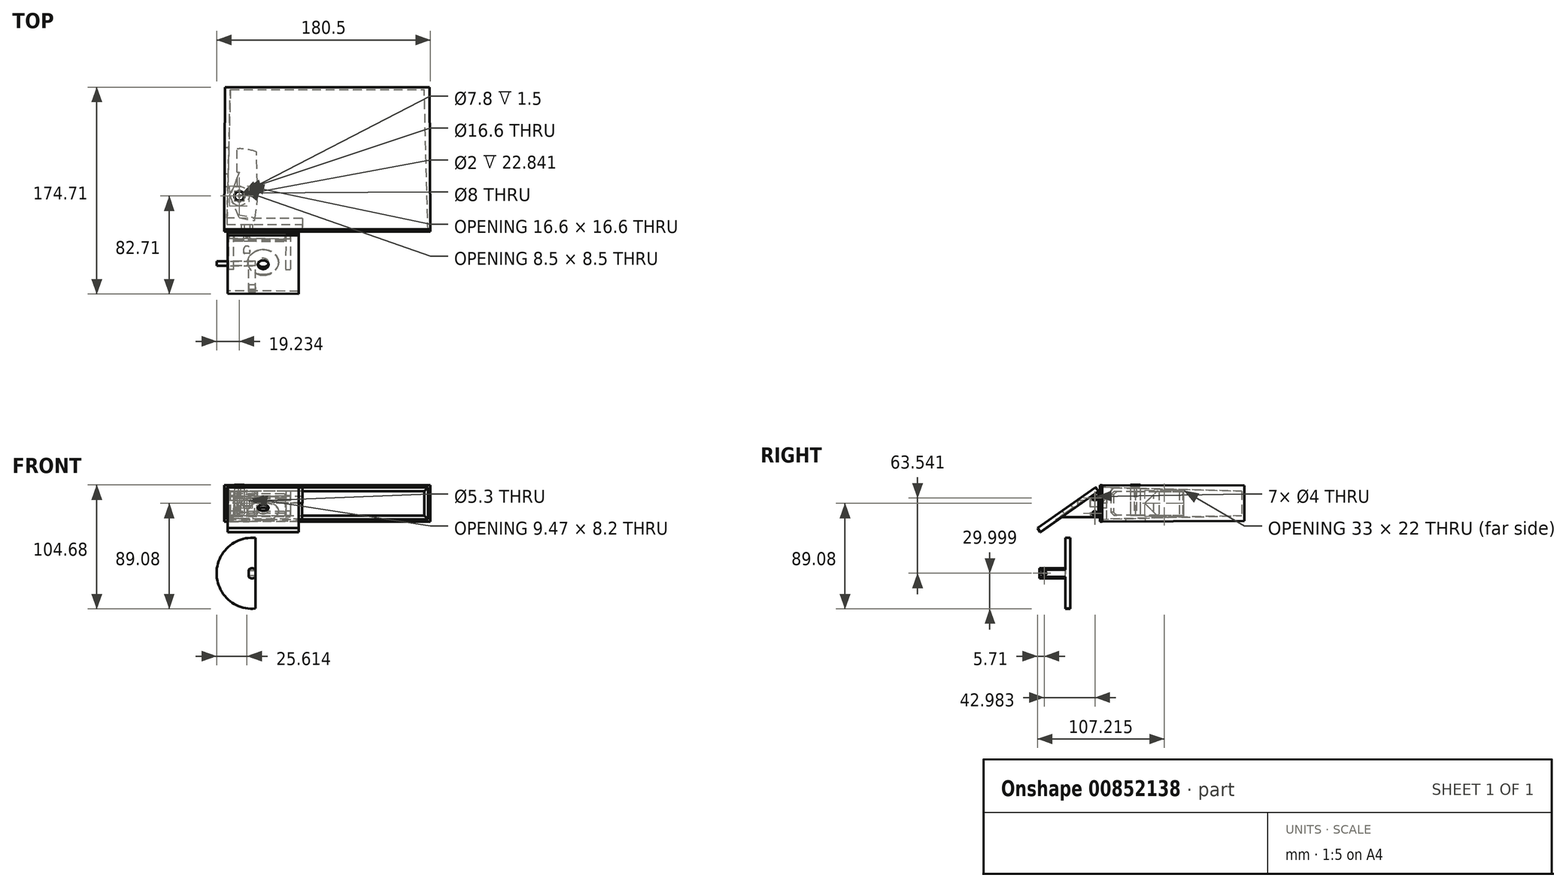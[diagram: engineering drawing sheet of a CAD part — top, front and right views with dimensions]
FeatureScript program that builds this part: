
annotation { "Feature Type Name" : "Feature", "Feature Type Description" : "" }
export const myFeature = defineFeature(function(context is Context, id is Id, definition is map)
    precondition{}
    {
        {
            var Q0;
            Q0=qCreatedBy(makeId("Front.planeOp"),FACE);
            cPlane(context, id + "F0", {"entities" : qUnion([Q0]), "cplaneType" : CPlaneType.OFFSET, "offset" : 25 * mm, "width" : 150 * mm, "height" : 150 * mm});
        }
        {
            var Q0;
            Q0=qCreatedBy(makeId("Top.planeOp"),FACE);
            cPlane(context, id + "F1", {"entities" : qUnion([Q0]), "cplaneType" : CPlaneType.OFFSET, "offset" : 25 * mm, "width" : 150 * mm, "height" : 150 * mm});
        }
        {
            var Q0;
            Q0=qCreatedBy(makeId("Top.planeOp"),FACE);
            cPlane(context, id + "F2", {"entities" : qUnion([Q0]), "cplaneType" : CPlaneType.OFFSET, "offset" : 24 * mm, "oppositeDirection" : true, "width" : 150 * mm, "height" : 150 * mm});
        }
        {
            var Q0;
            Q0=qCreatedBy(makeId("Right.planeOp"),FACE);
            cPlane(context, id + "F3", {"entities" : qUnion([Q0]), "cplaneType" : CPlaneType.OFFSET, "offset" : 45 * mm, "oppositeDirection" : true, "width" : 150 * mm, "height" : 150 * mm});
        }
        {
            var Q0;
            Q0=qCreatedBy(makeId("Front.planeOp"),FACE);
            var sketch = newSketch(context, id + "F4", { "sketchPlane" : qUnion([Q0])});
            skLineSegment(sketch, "E0.bottom", {"start": v(85, -13.5) * mm, "end": v(-85, -13.5) * mm});
            skLineSegment(sketch, "E0.top", {"start": v(85, 13.5) * mm, "end": v(-85, 13.5) * mm});
            skLineSegment(sketch, "E0.left", {"start": v(85, -13.5) * mm, "end": v(85, 13.5) * mm});
            skLineSegment(sketch, "E0.right", {"start": v(-85, -13.5) * mm, "end": v(-85, 13.5) * mm});
            skPoint(sketch, "E0.middle", {"position": v(0, 0) * mm});
            skLineSegment(sketch, "E1.0", {"start": v(87, 15.5) * mm, "end": v(-87, 15.5) * mm});
            skLineSegment(sketch, "E1.1", {"start": v(87, -15.5) * mm, "end": v(87, 15.5) * mm});
            skLineSegment(sketch, "E1.2", {"start": v(87, -15.5) * mm, "end": v(-87, -15.5) * mm});
            skLineSegment(sketch, "E1.3", {"start": v(-87, -15.5) * mm, "end": v(-87, 15.5) * mm});
            skLineSegment(sketch, "E2.0", {"start": v(91, 19.5) * mm, "end": v(-91, 19.5) * mm});
            skLineSegment(sketch, "E2.1", {"start": v(91, -19.5) * mm, "end": v(91, 19.5) * mm});
            skLineSegment(sketch, "E2.2", {"start": v(91, -19.5) * mm, "end": v(-91, -19.5) * mm});
            skLineSegment(sketch, "E2.3", {"start": v(-91, -19.5) * mm, "end": v(-91, 19.5) * mm});
            skSolve(sketch);
        }
        {
            var Q0;
            Q0=qCreatedBy(id+"F0.planeOp",FACE);
            var sketch = newSketch(context, id + "F5", { "sketchPlane" : qUnion([Q0])});
            skArc(sketch, "E3", {"start": v(-60.6, -29.22) * mm, "mid": v(-93.5, -59.08) * mm, "end": v(-60.6, -88.94) * mm});
            skArc(sketch, "E4", {"start": v(-60.6, -55.97) * mm, "mid": v(-63.5, -54.83) * mm, "end": v(-66.4, -55.97) * mm});
            skLineSegment(sketch, "E5.left", {"start": v(-60.6, -62.19) * mm, "end": v(-60.6, -55.97) * mm});
            skLineSegment(sketch, "E5.right", {"start": v(-66.4, -62.19) * mm, "end": v(-66.4, -55.97) * mm});
            skArc(sketch, "E6.trimOffspring", {"start": v(-66.4, -62.19) * mm, "mid": v(-63.5, -63.33) * mm, "end": v(-60.6, -62.19) * mm});
            skLineSegment(sketch, "E7", {"start": v(-60.6, -55.97) * mm, "end": v(-60.6, -29.22) * mm});
            skLineSegment(sketch, "E8", {"start": v(-60.6, -62.19) * mm, "end": v(-60.6, -88.94) * mm});
            skSolve(sketch);
        }
        {
            var Q0;
            Q0=makeQuery(id+"F5.imprint","IMPRINT",FACE,{"disambiguationData":[TD([[makeQuery(id+"F5.imprint","IMPRINT",EDGE,{"derivedFrom":sQuery(id+"F5.wireOp",EDGE,"E3")}),1.0]])]});
            extrude(context, id + "F6", {"entities" : qUnion([Q0]), "depth" : 4 * mm, "offsetDistance" : 25 * mm});
        }
        {
            var Q0;
            Q0=makeQuery(id+"F5.imprint","IMPRINT",FACE,{"disambiguationData":[TD([[makeQuery(id+"F5.imprint","IMPRINT",EDGE,{"derivedFrom":sQuery(id+"F5.wireOp",EDGE,"E4")}),1.0]])]});
            extrude(context, id + "F7", {"entities" : qUnion([Q0]), "operationType" : NewBodyOperationType.ADD, "depth" : 26 * mm, "offsetDistance" : 25 * mm});
        }
        {
            var Q0;
            Q0=makeQuery(id+"F7.opExtrude","SWEPT_FACE",FACE,{"disambiguationData":[OSD([sQuery(id+"F5.wireOp",EDGE,"E5.right")])]});
            cPlane(context, id + "F8", {"entities" : qUnion([Q0]), "cplaneType" : CPlaneType.OFFSET, "offset" : 0 * mm, "width" : 150 * mm, "height" : 150 * mm});
        }
        {
            var Q0;
            Q0=qCreatedBy(id+"F8.planeOp",FACE);
            var sketch = newSketch(context, id + "F9", { "sketchPlane" : qUnion([Q0])});
            skLineSegment(sketch, "E9.0.0", {"start": v(29, -55.97) * mm, "end": v(29, -62.19) * mm, "construction": true});
            skLineSegment(sketch, "E9.0.1", {"start": v(29, -62.19) * mm, "end": v(51, -62.19) * mm, "construction": true});
            skLineSegment(sketch, "E9.0.2", {"start": v(51, -62.19) * mm, "end": v(51, -55.97) * mm, "construction": true});
            skLineSegment(sketch, "E9.0.3", {"start": v(51, -55.97) * mm, "end": v(29, -55.97) * mm, "construction": true});
            skLineSegment(sketch, "E10", {"start": v(51, -59.08) * mm, "end": v(47, -59.08) * mm, "construction": true});
            skCircle(sketch, "E11", {"center": v(47, -59.08) * mm, "radius": 2 * mm});
            skSolve(sketch);
        }
        {
            var Q0;
            Q0=makeQuery(id+"F9.imprint","IMPRINT",FACE,{"disambiguationData":[TD([[makeQuery(id+"F9.imprint","IMPRINT",EDGE,{"derivedFrom":sQuery(id+"F9.wireOp",EDGE,"E11")}),1.0]])]});
            extrude(context, id + "F10", {"entities" : qUnion([Q0]), "operationType" : NewBodyOperationType.REMOVE, "endBound" : BoundingType.THROUGH_ALL, "oppositeDirection" : true, "depth" : 25 * mm, "offsetDistance" : 25 * mm});
        }
        {
            var Q0;
            Q0=makeQuery(id+"F4.imprint","IMPRINT",FACE,{"disambiguationData":[TD([[makeQuery(id+"F4.imprint","IMPRINT",EDGE,{"derivedFrom":sQuery(id+"F4.wireOp",EDGE,"E1.0")}),-1.0]])]});
            extrude(context, id + "F11", {"entities" : qUnion([Q0]), "oppositeDirection" : true, "depth" : 2 * mm, "offsetDistance" : 25 * mm});
        }
        {
            var Q0;
            Q0=makeQuery(id+"F4.imprint","IMPRINT",FACE,{"disambiguationData":[TD([[makeQuery(id+"F4.imprint","IMPRINT",EDGE,{"derivedFrom":sQuery(id+"F4.wireOp",EDGE,"E0.bottom")}),1.0]])]});
            var Q1;
            Q1=makeQuery(id+"F4.imprint","IMPRINT",FACE,{"disambiguationData":[TD([[makeQuery(id+"F4.imprint","IMPRINT",EDGE,{"derivedFrom":sQuery(id+"F4.wireOp",EDGE,"E0.bottom")}),-1.0]])]});
            extrude(context, id + "F12", {"entities" : qUnion([Q0, Q1]), "operationType" : NewBodyOperationType.ADD, "oppositeDirection" : true, "depth" : 122 * mm, "offsetDistance" : 25 * mm, "hasDraft" : true, "draftAngle" : .25 * degree, "draftPullDirection" : true});
        }
        {
            var Q0;
            Q0=makeQuery(id+"F4.imprint","IMPRINT",FACE,{"disambiguationData":[TD([[makeQuery(id+"F4.imprint","IMPRINT",EDGE,{"derivedFrom":sQuery(id+"F4.wireOp",EDGE,"E0.bottom")}),-1.0]])]});
            extrude(context, id + "F13", {"entities" : qUnion([Q0]), "operationType" : NewBodyOperationType.REMOVE, "oppositeDirection" : true, "depth" : 120 * mm, "offsetDistance" : 25 * mm, "hasDraft" : true, "draftAngle" : 1.5 * degree, "draftPullDirection" : true});
        }
        {
            var Q0;
            Q0=makeQuery(id+"F12.opExtrude","SWEPT_FACE",FACE,{"disambiguationData":[OSD([sQuery(id+"F4.wireOp",EDGE,"E1.3")])]});
            var sketch = newSketch(context, id + "F14", { "sketchPlane" : qUnion([Q0])});
            skPoint(sketch, "E12.2", {"position": v(-121.62, 0) * mm});
            skLineSegment(sketch, "E13", {"start": v(0, 15.5) * mm, "end": v(0, -15.5) * mm, "construction": true});
            skLineSegment(sketch, "E14", {"start": v(-121.62, 14.97) * mm, "end": v(-121.62, -14.97) * mm});
            skSolve(sketch);
        }
        {
            var Q0;
            Q0=qCreatedBy(makeId("Top.planeOp"),FACE);
            var sketch = newSketch(context, id + "F15", { "sketchPlane" : qUnion([Q0])});
            skLineSegment(sketch, "E15.0", {"start": v(86.47, 122) * mm, "end": v(-86.47, 122) * mm, "construction": true});
            skLineSegment(sketch, "E16", {"start": v(-43.53, 122) * mm, "end": v(-43.53, 120) * mm, "construction": true});
            skLineSegment(sketch, "E17", {"start": v(-87, 10.81) * mm, "end": v(-87, 17.59) * mm});
            skLineSegment(sketch, "E18", {"start": v(-86.47, 122) * mm, "end": v(-92.46, 2347.34) * mm, "construction": true});
            skLineSegment(sketch, "E19", {"start": v(-92.46, 2347.34) * mm, "end": v(-62.46, 2347.34) * mm, "construction": true});
            skLineSegment(sketch, "E20", {"start": v(-62.46, 2347.34) * mm, "end": v(-62.46, -10.74) * mm, "construction": true});
            skLineSegment(sketch, "E21", {"start": v(-86.47, 122) * mm, "end": v(-62.46, 0) * mm, "construction": true});
            skLineSegment(sketch, "E22", {"start": v(-62.46, 0) * mm, "end": v(-87, 0) * mm, "construction": true});
            skLineSegment(sketch, "E23", {"start": v(-74.27, 60) * mm, "end": v(-103.47, 60) * mm, "construction": true});
            skLineSegment(sketch, "E24", {"start": v(-92.32, 0) * mm, "end": v(-92.32, 30) * mm, "construction": true});
            skLineSegment(sketch, "E25", {"start": v(-92.32, 30) * mm, "end": v(-50.7, 30) * mm, "construction": true});
            skLineSegment(sketch, "E26", {"start": v(-74.27, 60) * mm, "end": v(-74.27, -24.78) * mm, "construction": true});
            skCircle(sketch, "E27", {"center": v(-74.27, 30) * mm, "radius": 4 * mm});
            skCircle(sketch, "E28", {"center": v(-74.27, 30) * mm, "radius": 3.3 * mm});
            skLineSegment(sketch, "E29", {"start": v(-74.27, 60) * mm, "end": v(-87, 60) * mm});
            skLineSegment(sketch, "E30", {"start": v(-87, 50) * mm, "end": v(-74.31, 50) * mm});
            skLineSegment(sketch, "E31", {"start": v(-74.27, 11.6) * mm, "end": v(-43.55, 11.6) * mm, "construction": true});
            skLineSegment(sketch, "E32", {"start": v(-74.27, 11.6) * mm, "end": v(-61.5, 9.34) * mm});
            skArc(sketch, "E33.trimOffspring", {"start": v(-72.46, 0) * mm, "mid": v(-70.93, -0.04) * mm, "end": v(-69.4, 0) * mm});
            skLineSegment(sketch, "E34.MirrorCS", {"start": v(-87, 70) * mm, "end": v(-74.31, 70) * mm});
            skArc(sketch, "E35", {"start": v(-59.68, 67.25) * mm, "mid": v(-66.87, 69.32) * mm, "end": v(-74.31, 70) * mm});
            skLineSegment(sketch, "E36", {"start": v(-58.9, 30) * mm, "end": v(-61.5, 9.34) * mm});
            skLineSegment(sketch, "E37.trimOffspring", {"start": v(-64.4, 9.85) * mm, "end": v(-62.46, 9.51) * mm});
            skLineSegment(sketch, "E38", {"start": v(-58.9, 30) * mm, "end": v(-59.68, 67.25) * mm});
            skLineSegment(sketch, "E39", {"start": v(-87, 70) * mm, "end": v(-87, 50) * mm});
            skLineSegment(sketch, "E40.0", {"start": v(91, 2) * mm, "end": v(-91, 2) * mm, "construction": true});
            skLineSegment(sketch, "E41", {"start": v(-74.31, 50) * mm, "end": v(-82.27, 30) * mm});
            skLineSegment(sketch, "E42", {"start": v(-82.27, 30) * mm, "end": v(-74.27, 11.6) * mm});
            skSolve(sketch);
        }
        {
            var Q0;
            {var subQ2=sQuery(id+"F15.wireOp",EDGE,"E27");Q0=makeQuery(id+"F15.imprint","IMPRINT",FACE,{"disambiguationData":[TD([[makeQuery(id+"F15.imprint","IMPRINT",EDGE,{"derivedFrom":subQ2}),-1.0]])]});}
            extrude(context, id + "F16", {"entities" : qUnion([Q0]), "endBound" : BoundingType.SYMMETRIC, "depth" : 20 * mm, "offsetDistance" : 25 * mm});
        }
        {
            var Q0;
            Q0=qCreatedBy(id+"F3.planeOp",FACE);
            var sketch = newSketch(context, id + "F17", { "sketchPlane" : qUnion([Q0])});
            skLineSegment(sketch, "E43.0.0", {"start": v(70, -10) * mm, "end": v(50, -10) * mm, "construction": true});
            skLineSegment(sketch, "E43.0.1", {"start": v(50, -10) * mm, "end": v(50, 10) * mm, "construction": true});
            skLineSegment(sketch, "E43.0.2", {"start": v(50, 10) * mm, "end": v(70, 10) * mm, "construction": true});
            skLineSegment(sketch, "E43.0.3", {"start": v(70, 10) * mm, "end": v(70, -10) * mm, "construction": true});
            skLineSegment(sketch, "E44.0", {"start": v(71, 11) * mm, "end": v(71, -11) * mm});
            skLineSegment(sketch, "E44.1", {"start": v(49, 11) * mm, "end": v(71, 11) * mm});
            skLineSegment(sketch, "E44.2", {"start": v(49, -11) * mm, "end": v(49, 11) * mm, "construction": true});
            skLineSegment(sketch, "E44.3", {"start": v(71, -11) * mm, "end": v(49, -11) * mm});
            skLineSegment(sketch, "E45", {"start": v(49, 11) * mm, "end": v(38, 0) * mm});
            skPoint(sketch, "E45.endSnap0", {"position": v(49, 0) * mm});
            skLineSegment(sketch, "E46", {"start": v(38, 0) * mm, "end": v(49, -11) * mm});
            skSolve(sketch);
        }
        {
            var Q0;
            Q0=makeQuery(id+"F17.imprint","IMPRINT",FACE,{"disambiguationData":[TD([[makeQuery(id+"F17.imprint","IMPRINT",EDGE,{"derivedFrom":sQuery(id+"F17.wireOp",EDGE,"E44.0")}),-1.0]])]});
            extrude(context, id + "F18", {"entities" : qUnion([Q0]), "operationType" : NewBodyOperationType.REMOVE, "oppositeDirection" : true, "depth" : 49.1 * mm, "offsetDistance" : 25 * mm, "hasSecondDirection" : true, "secondDirectionOppositeDirection" : true, "secondDirectionDepth" : 31.1 * mm});
        }
        {
            var Q0;
            Q0=qCreatedBy(id+"F2.planeOp",FACE);
            var sketch = newSketch(context, id + "F19", { "sketchPlane" : qUnion([Q0])});
            skCircle(sketch, "E47", {"center": v(-74.27, 30) * mm, "radius": 4.25 * mm});
            skCircle(sketch, "E48", {"center": v(-74.27, 30) * mm, "radius": 1 * mm});
            skCircle(sketch, "E49.0", {"center": v(-74.27, 30) * mm, "radius": 4 * mm, "construction": true});
            skCircle(sketch, "E50", {"center": v(-74.27, 30) * mm, "radius": 8 * mm});
            skCircle(sketch, "E51.0", {"center": v(-74.27, 30) * mm, "radius": 8.3 * mm});
            skSolve(sketch);
        }
        {
            var Q0;
            Q0=makeQuery(id+"F19.imprint","IMPRINT",FACE,{"disambiguationData":[TD([[makeQuery(id+"F19.imprint","IMPRINT",EDGE,{"derivedFrom":sQuery(id+"F19.wireOp",EDGE,"E47")}),1.0]])]});
            extrude(context, id + "F20", {"entities" : qUnion([Q0]), "depth" : 39.6 * mm, "offsetDistance" : 25 * mm, "hasSecondDirection" : true, "secondDirectionOppositeDirection" : false, "secondDirectionDepth" : 8.6 * mm});
        }
        {
            var Q0;
            Q0=makeQuery(id+"F19.imprint","IMPRINT",FACE,{"disambiguationData":[TD([[makeQuery(id+"F19.imprint","IMPRINT",EDGE,{"derivedFrom":sQuery(id+"F19.wireOp",EDGE,"E47")}),-1.0]])]});
            extrude(context, id + "F21", {"entities" : qUnion([Q0]), "operationType" : NewBodyOperationType.ADD, "depth" : 13.9 * mm, "offsetDistance" : 25 * mm, "hasSecondDirection" : true, "secondDirectionOppositeDirection" : false, "secondDirectionDepth" : 8.9 * mm});
        }
        {
            var Q0;
            Q0=qCreatedBy(id+"F1.planeOp",FACE);
            var sketch = newSketch(context, id + "F22", { "sketchPlane" : qUnion([Q0])});
            skCircle(sketch, "E52", {"center": v(-74.27, 30) * mm, "radius": 3.9 * mm});
            skLineSegment(sketch, "E53.0.1", {"start": v(91, 0) * mm, "end": v(91, 2) * mm, "construction": true});
            skLineSegment(sketch, "E53.0.3", {"start": v(-91, 2) * mm, "end": v(-91, 0) * mm, "construction": true});
            skLineSegment(sketch, "E54", {"start": v(-21.12, 2) * mm, "end": v(-85.12, 2) * mm});
            skLineSegment(sketch, "E55", {"start": v(-85.12, 6) * mm, "end": v(-21.12, 6) * mm});
            skCircle(sketch, "E56.0", {"center": v(-74.27, 30) * mm, "radius": 4 * mm, "construction": true});
            skLineSegment(sketch, "E57", {"start": v(-85.12, 2) * mm, "end": v(-85.12, 6) * mm});
            skLineSegment(sketch, "E58", {"start": v(-21.12, 6) * mm, "end": v(-21.12, 2) * mm});
            skSolve(sketch);
        }
        {
            var Q0;
            Q0=makeQuery(id+"F22.imprint","IMPRINT",FACE,{"disambiguationData":[TD([[makeQuery(id+"F22.imprint","IMPRINT",EDGE,{"derivedFrom":sQuery(id+"F22.wireOp",EDGE,"E52")}),1.0]])]});
            extrude(context, id + "F23", {"entities" : qUnion([Q0]), "operationType" : NewBodyOperationType.REMOVE, "oppositeDirection" : true, "depth" : 10.9 * mm, "offsetDistance" : 25 * mm});
        }
        {
            var Q0;
            Q0=qCreatedBy(id+"F1.planeOp",FACE);
            var sketch = newSketch(context, id + "F24", { "sketchPlane" : qUnion([Q0])});
            skCircle(sketch, "E59.0", {"center": v(-74.27, 30) * mm, "radius": 2.5 * mm, "construction": true});
            skCircle(sketch, "E60", {"center": v(-74.27, 30) * mm, "radius": 2.2 * mm});
            skCircle(sketch, "E61", {"center": v(-74.27, 30) * mm, "radius": 3.75 * mm});
            skCircle(sketch, "E62.0", {"center": v(-74.27, 30) * mm, "radius": 4 * mm, "construction": true});
            skCircle(sketch, "E63", {"center": v(-74.27, 30) * mm, "radius": 1 * mm});
            skSolve(sketch);
        }
        {
            var Q0;
            Q0=makeQuery(id+"F16.opExtrude","CAP_EDGE",EDGE,{"disambiguationData":[OSD([sQuery(id+"F15.wireOp",EDGE,"E32"),sQuery(id+"F15.wireOp",EDGE,"E37.trimOffspring")])],"isStart":false});
            var Q1;
            Q1=makeQuery(id+"F16.opExtrude","CAP_EDGE",EDGE,{"disambiguationData":[OSD([sQuery(id+"F15.wireOp",EDGE,"E32"),sQuery(id+"F15.wireOp",EDGE,"E37.trimOffspring")])],"isStart":true});
            chamfer(context, id + "F25", {"entities" : qUnion([Q0, Q1]), "width" : 2.5 * mm, "tangentPropagation" : true});
        }
        {
            var Q0;
            Q0=makeQuery(id+"F22.imprint","IMPRINT",FACE,{"disambiguationData":[TD([[makeQuery(id+"F22.imprint","IMPRINT",EDGE,{"derivedFrom":sQuery(id+"F22.wireOp",EDGE,"E54")}),-1.0]])]});
            extrude(context, id + "F26", {"entities" : qUnion([Q0]), "operationType" : NewBodyOperationType.ADD, "oppositeDirection" : true, "depth" : 40.1 * mm, "offsetDistance" : 25 * mm, "hasSecondDirection" : true, "secondDirectionOppositeDirection" : true, "secondDirectionDepth" : 10.8 * mm});
        }
        {
            var Q0;
            Q0=makeQuery(id+"F12.opExtrude","SWEPT_FACE",FACE,{"disambiguationData":[OSD([sQuery(id+"F4.wireOp",EDGE,"E1.3")])]});
            var sketch = newSketch(context, id + "F27", { "sketchPlane" : qUnion([Q0])});
            skLineSegment(sketch, "E64.0", {"start": v(-1.6, -19.5) * mm, "end": v(-1.6, 19.5) * mm, "construction": true});
            skPoint(sketch, "E65.2", {"position": v(-9.08, 0) * mm});
            skLineSegment(sketch, "E66", {"start": v(-121.62, -14.97) * mm, "end": v(-121.62, 14.97) * mm, "construction": true});
            skLineSegment(sketch, "E67", {"start": v(-12.52, 15.44) * mm, "end": v(-1.6, 0) * mm});
            skPoint(sketch, "E68.orphan", {"position": v(0.56, -3.07) * mm});
            skPoint(sketch, "E69.orphan", {"position": v(-1.57, 6.86) * mm});
            skLineSegment(sketch, "E70", {"start": v(-12.52, 15.44) * mm, "end": v(0.38, 15.5) * mm});
            skLineSegment(sketch, "E71", {"start": v(0.38, 15.5) * mm, "end": v(0.38, -15.5) * mm});
            skLineSegment(sketch, "E72", {"start": v(0.38, -15.5) * mm, "end": v(-12.52, -15.44) * mm});
            skLineSegment(sketch, "E73", {"start": v(-1.6, 0) * mm, "end": v(-12.52, -15.44) * mm});
            skSolve(sketch);
        }
        {
            var Q0;
            Q0=makeQuery(id+"F27.imprint","IMPRINT",FACE,{"disambiguationData":[TD([[makeQuery(id+"F27.imprint","IMPRINT",EDGE,{"derivedFrom":sQuery(id+"F27.wireOp",EDGE,"E67")}),1.0]])]});
            extrude(context, id + "F28", {"entities" : qUnion([Q0]), "operationType" : NewBodyOperationType.ADD, "oppositeDirection" : true, "depth" : 66 * mm, "offsetDistance" : 25 * mm});
        }
        {
            var Q0;
            Q0=makeQuery(id+"F4.imprint","IMPRINT",FACE,{"disambiguationData":[TD([[makeQuery(id+"F4.imprint","IMPRINT",EDGE,{"derivedFrom":sQuery(id+"F4.wireOp",EDGE,"E1.0")}),-1.0]])]});
            extrude(context, id + "F29", {"entities" : qUnion([Q0]), "operationType" : NewBodyOperationType.REMOVE, "oppositeDirection" : true, "depth" : 25 * mm, "offsetDistance" : 25 * mm});
        }
        {
            var Q0;
            Q0=makeQuery(id+"F12.opExtrude","SWEPT_FACE",FACE,{"disambiguationData":[OSD([sQuery(id+"F4.wireOp",EDGE,"E1.3")])]});
            var sketch = newSketch(context, id + "F30", { "sketchPlane" : qUnion([Q0])});
            skLineSegment(sketch, "E74.0.0", {"start": v(-0.37, -13.5) * mm, "end": v(-0.37, 13.5) * mm, "construction": true});
            skLineSegment(sketch, "E74.0.2", {"start": v(0.37, 13.5) * mm, "end": v(0.37, -13.5) * mm, "construction": true});
            skLineSegment(sketch, "E75", {"start": v(-0.37, -13.5) * mm, "end": v(5.95, -13.5) * mm, "construction": true});
            skLineSegment(sketch, "E76", {"start": v(52.81, -20.91) * mm, "end": v(50.52, -24.2) * mm});
            skLineSegment(sketch, "E77", {"start": v(1.37, -13.5) * mm, "end": v(1.37, -11.5) * mm, "construction": true});
            skLineSegment(sketch, "E78", {"start": v(-0.37, 13.5) * mm, "end": v(1.37, 13.5) * mm, "construction": true});
            skLineSegment(sketch, "E79.0", {"start": v(3.67, 13.5) * mm, "end": v(52.81, -20.91) * mm});
            skLineSegment(sketch, "E80", {"start": v(3.67, 13.5) * mm, "end": v(1.37, 10.22) * mm});
            skLineSegment(sketch, "E81", {"start": v(1.37, 10.22) * mm, "end": v(50.52, -24.2) * mm});
            skLineSegment(sketch, "E82", {"start": v(1.37, 10.22) * mm, "end": v(1.37, -11.5) * mm});
            skLineSegment(sketch, "E83", {"start": v(32.4, -11.5) * mm, "end": v(1.37, -11.5) * mm});
            skCircle(sketch, "E84", {"center": v(4.37, -8.5) * mm, "radius": 3 * mm, "construction": true});
            skPoint(sketch, "E84.first.point", {"position": v(1.37, -8.5) * mm});
            skPoint(sketch, "E84.second.point", {"position": v(4.37, -11.5) * mm});
            skPoint(sketch, "E84.third.point", {"position": v(7.3, -9.1) * mm});
            skCircle(sketch, "E85", {"center": v(4.37, 4.46) * mm, "radius": 3 * mm, "construction": true});
            skPoint(sketch, "E85.first.point", {"position": v(1.37, 4.46) * mm});
            skPoint(sketch, "E85.second.point", {"position": v(6.1, 6.92) * mm});
            skPoint(sketch, "E85.third.point", {"position": v(6.92, 2.88) * mm});
            skCircle(sketch, "E86", {"center": v(4.37, 4.46) * mm, "radius": 2 * mm});
            skCircle(sketch, "E87", {"center": v(4.37, -8.5) * mm, "radius": 2 * mm});
            skSolve(sketch);
        }
        {
            var Q0;
            {var subQ3=sQuery(id+"F30.wireOp",EDGE,"E76");Q0=makeQuery(id+"F30.imprint","IMPRINT",FACE,{"disambiguationData":[TD([[makeQuery(id+"F30.imprint","IMPRINT",EDGE,{"derivedFrom":subQ3}),-1.0]])]});}
            extrude(context, id + "F31", {"entities" : qUnion([Q0]), "oppositeDirection" : true, "depth" : 63 * mm, "offsetDistance" : 25 * mm, "hasSecondDirection" : true, "secondDirectionOppositeDirection" : true, "secondDirectionDepth" : 3 * mm});
        }
        {
            var Q0;
            {var subQ1=sQuery(id+"F30.wireOp",EDGE,"E82");Q0=makeQuery(id+"F30.imprint","IMPRINT",FACE,{"disambiguationData":[TD([[makeQuery(id+"F30.imprint","IMPRINT",EDGE,{"derivedFrom":subQ1}),1.0]])]});}
            extrude(context, id + "F32", {"entities" : qUnion([Q0]), "operationType" : NewBodyOperationType.ADD, "oppositeDirection" : true, "depth" : 56 * mm, "offsetDistance" : 25 * mm, "hasSecondDirection" : true, "secondDirectionOppositeDirection" : true, "secondDirectionDepth" : 52 * mm});
        }
        {
            var Q0;
            Q0 = qSketchRegion(id + "F30", true);
            extrude(context, id + "F33", {"entities" : qUnion([Q0]), "operationType" : NewBodyOperationType.ADD, "oppositeDirection" : true, "depth" : 8 * mm, "offsetDistance" : 25 * mm, "hasSecondDirection" : true, "secondDirectionOppositeDirection" : true, "secondDirectionDepth" : 4 * mm});
        }
        {
            var Q0;
            Q0=makeQuery(id+"F31.opExtrude","SWEPT_FACE",FACE,{"disambiguationData":[OSD([sQuery(id+"F30.wireOp",EDGE,"E79.0")])]});
            var sketch = newSketch(context, id + "F34", { "sketchPlane" : qUnion([Q0])});
            skLineSegment(sketch, "E88.0.0", {"start": v(-23.98, 4.83) * mm, "end": v(-83.98, 5.04) * mm, "construction": true});
            skLineSegment(sketch, "E88.0.1", {"start": v(-83.98, 5.04) * mm, "end": v(-84.2, -54.96) * mm, "construction": true});
            skLineSegment(sketch, "E88.0.2", {"start": v(-84.2, -54.96) * mm, "end": v(-24.2, -55.17) * mm, "construction": true});
            skLineSegment(sketch, "E88.0.3", {"start": v(-24.2, -55.17) * mm, "end": v(-23.98, 4.83) * mm, "construction": true});
            skLineSegment(sketch, "E89", {"start": v(-83.98, 5.04) * mm, "end": v(-24.2, -55.17) * mm, "construction": true});
            skCircle(sketch, "E90", {"center": v(-54.09, -25.07) * mm, "radius": 4.5 * mm});
            skCircle(sketch, "E91", {"center": v(-54.09, -25.07) * mm, "radius": 13 * mm});
            skSolve(sketch);
        }
        {
            var Q0;
            Q0=makeQuery(id+"F34.imprint","IMPRINT",FACE,{"disambiguationData":[TD([[makeQuery(id+"F34.imprint","IMPRINT",EDGE,{"derivedFrom":sQuery(id+"F34.wireOp",EDGE,"E90")}),1.0]])]});
            var Q1;
            Q1=sQuery(id+"F34.wireOp",EDGE,"E90");
            extrude(context, id + "F35", {"entities" : qUnion([Q0]), "operationType" : NewBodyOperationType.REMOVE, "surfaceEntities" : qUnion([Q1]), "oppositeDirection" : true, "depth" : 8.8 * mm, "offsetDistance" : 25 * mm});
        }
        {
            var Q0;
            Q0=makeQuery(id+"F34.imprint","IMPRINT",FACE,{"disambiguationData":[TD([[makeQuery(id+"F34.imprint","IMPRINT",EDGE,{"derivedFrom":sQuery(id+"F34.wireOp",EDGE,"E90")}),-1.0]])]});
            extrude(context, id + "F36", {"entities" : qUnion([Q0]), "operationType" : NewBodyOperationType.REMOVE, "oppositeDirection" : true, "depth" : 34.3 * mm, "offsetDistance" : 25 * mm, "hasSecondDirection" : true, "secondDirectionOppositeDirection" : true, "secondDirectionDepth" : 3 * mm});
        }
        {
            var Q0;
            Q0=makeQuery(id+"F32.opExtrude","CAP_FACE",FACE,{"disambiguationData":[OSD([sQuery(id+"F30.wireOp",EDGE,"E81"),sQuery(id+"F30.wireOp",EDGE,"E82"),sQuery(id+"F30.wireOp",EDGE,"E83"),sQuery(id+"F30.wireOp",EDGE,"E86"),sQuery(id+"F30.wireOp",EDGE,"E87")])],"isStart":false});
            var sketch = newSketch(context, id + "F37", { "sketchPlane" : qUnion([Q0])});
            skCircle(sketch, "E92.0", {"center": v(-4.37, 4.46) * mm, "radius": 2 * mm});
            skCircle(sketch, "E92.1", {"center": v(-4.37, -8.5) * mm, "radius": 2 * mm});
            skLineSegment(sketch, "E92.2", {"start": v(-1.37, 10.22) * mm, "end": v(-1.37, -11.5) * mm, "construction": true});
            skLineSegment(sketch, "E92.3", {"start": v(-1.37, 10.22) * mm, "end": v(-50.52, -24.2) * mm, "construction": true});
            skLineSegment(sketch, "E92.4", {"start": v(-32.4, -11.5) * mm, "end": v(-1.37, -11.5) * mm, "construction": true});
            skLineSegment(sketch, "E93.0", {"start": v(-0.37, 10.22) * mm, "end": v(-0.37, -11.5) * mm, "construction": true});
            skArc(sketch, "E94", {"start": v(-0.37, 4.46) * mm, "mid": v(-1.25, 6.96) * mm, "end": v(-3.5, 8.36) * mm});
            skArc(sketch, "E95", {"start": v(-8.36, -8.08) * mm, "mid": v(-8.2, -9.7) * mm, "end": v(-7.41, -11.11) * mm});
            skLineSegment(sketch, "E96", {"start": v(-0.37, 4.46) * mm, "end": v(-0.37, -8.23) * mm});
            skLineSegment(sketch, "E97", {"start": v(-8.36, 4.14) * mm, "end": v(-8.36, -8.08) * mm});
            skLineSegment(sketch, "E98", {"start": v(-8.34, 4.97) * mm, "end": v(-3.5, 8.36) * mm});
            skLineSegment(sketch, "E99", {"start": v(-7.41, -11.11) * mm, "end": v(-1.33, -11.11) * mm});
            skArc(sketch, "E100.trimOffspring", {"start": v(-8.34, 4.97) * mm, "mid": v(-8.37, 4.56) * mm, "end": v(-8.36, 4.14) * mm});
            skArc(sketch, "E101.trimOffspring", {"start": v(-1.37, -11.16) * mm, "mid": v(-0.58, -9.8) * mm, "end": v(-0.37, -8.23) * mm});
            skCircle(sketch, "E102.0", {"center": v(-4.37, 4.46) * mm, "radius": 1.7 * mm});
            skSolve(sketch);
        }
        {
            var Q0;
            {var subQ5=sQuery(id+"F37.wireOp",EDGE,"E96");Q0=makeQuery(id+"F37.imprint","IMPRINT",FACE,{"disambiguationData":[TD([[makeQuery(id+"F37.imprint","IMPRINT",EDGE,{"derivedFrom":subQ5}),-1.0]])]});}
            var Q1;
            Q1=makeQuery(id+"F37.imprint","IMPRINT",FACE,{"disambiguationData":[TD([[makeQuery(id+"F37.imprint","IMPRINT",EDGE,{"derivedFrom":sQuery(id+"F37.wireOp",EDGE,"E92.0")}),1.0]])]});
            extrude(context, id + "F38", {"entities" : qUnion([Q0, Q1]), "operationType" : NewBodyOperationType.ADD, "oppositeDirection" : true, "depth" : 47.5 * mm, "offsetDistance" : 25 * mm, "hasSecondDirection" : true, "secondDirectionOppositeDirection" : true, "secondDirectionDepth" : 4.5 * mm});
        }
        {
            var Q0;
            Q0=makeQuery(id+"F37.imprint","IMPRINT",FACE,{"disambiguationData":[TD([[makeQuery(id+"F37.imprint","IMPRINT",EDGE,{"derivedFrom":sQuery(id+"F37.wireOp",EDGE,"E102.0")}),1.0]])]});
            extrude(context, id + "F39", {"entities" : qUnion([Q0]), "oppositeDirection" : true, "depth" : 52 * mm, "offsetDistance" : 25 * mm});
        }
        {
            var Q0;
            Q0=makeQuery(id+"F4.imprint","IMPRINT",FACE,{"disambiguationData":[TD([[makeQuery(id+"F4.imprint","IMPRINT",EDGE,{"derivedFrom":sQuery(id+"F4.wireOp",EDGE,"E0.bottom")}),-1.0]])]});
            cPlane(context, id + "F40", {"entities" : qUnion([Q0]), "cplaneType" : CPlaneType.OFFSET, "offset" : 6 * mm, "width" : 150 * mm, "height" : 150 * mm});
        }
        {
            var Q0;
            Q0=qCreatedBy(id+"F40.planeOp",FACE);
            var sketch = newSketch(context, id + "F41", { "sketchPlane" : qUnion([Q0])});
            skLineSegment(sketch, "E103", {"start": v(-74.27, 7.5) * mm, "end": v(-61.5, -7.5) * mm, "construction": true});
            skCircle(sketch, "E104", {"center": v(-67.89, 0) * mm, "radius": 2.65 * mm});
            skLineSegment(sketch, "E105.0", {"start": v(-61.5, 7.5) * mm, "end": v(-74.27, 7.5) * mm, "construction": true});
            skLineSegment(sketch, "E105.1", {"start": v(-74.27, -7.5) * mm, "end": v(-61.5, -7.5) * mm, "construction": true});
            skCircle(sketch, "E106.cCircle", {"center": v(-67.89, 0) * mm, "radius": 4.1 * mm, "construction": true});
            skLineSegment(sketch, "E106.0", {"start": v(-65.52, 4.1) * mm, "end": v(-63.15, 0) * mm});
            skLineSegment(sketch, "E106.1", {"start": v(-63.15, 0) * mm, "end": v(-65.52, -4.1) * mm});
            skLineSegment(sketch, "E106.2", {"start": v(-65.52, -4.1) * mm, "end": v(-70.25, -4.1) * mm});
            skLineSegment(sketch, "E106.3", {"start": v(-70.25, -4.1) * mm, "end": v(-72.62, 0) * mm});
            skLineSegment(sketch, "E106.4", {"start": v(-72.62, 0) * mm, "end": v(-70.25, 4.1) * mm});
            skLineSegment(sketch, "E106.5", {"start": v(-70.25, 4.1) * mm, "end": v(-65.52, 4.1) * mm});
            skPoint(sketch, "E106.0.midPoint", {"position": v(-64.34, 2.05) * mm});
            skSolve(sketch);
        }
        {
            var Q0;
            Q0=makeQuery(id+"F41.imprint","IMPRINT",FACE,{"disambiguationData":[TD([[makeQuery(id+"F41.imprint","IMPRINT",EDGE,{"derivedFrom":sQuery(id+"F41.wireOp",EDGE,"E104")}),1.0]])]});
            extrude(context, id + "F42", {"entities" : qUnion([Q0]), "operationType" : NewBodyOperationType.REMOVE, "endBound" : BoundingType.SYMMETRIC, "depth" : 25 * mm, "offsetDistance" : 25 * mm});
        }
        {
            var Q0;
            Q0=makeQuery(id+"F19.imprint","IMPRINT",FACE,{"disambiguationData":[TD([[makeQuery(id+"F19.imprint","IMPRINT",EDGE,{"derivedFrom":sQuery(id+"F19.wireOp",EDGE,"E50")}),-1.0]])]});
            var Q1;
            Q1=makeQuery(id+"F19.imprint","IMPRINT",FACE,{"disambiguationData":[TD([[makeQuery(id+"F19.imprint","IMPRINT",EDGE,{"derivedFrom":sQuery(id+"F19.wireOp",EDGE,"E47")}),-1.0]])]});
            var Q2;
            Q2=makeQuery(id+"F19.imprint","IMPRINT",FACE,{"disambiguationData":[TD([[makeQuery(id+"F19.imprint","IMPRINT",EDGE,{"derivedFrom":sQuery(id+"F19.wireOp",EDGE,"E47")}),1.0]])]});
            var Q3;
            Q3=makeQuery(id+"F19.imprint","IMPRINT",FACE,{"disambiguationData":[TD([[makeQuery(id+"F19.imprint","IMPRINT",EDGE,{"derivedFrom":sQuery(id+"F19.wireOp",EDGE,"E48")}),1.0]])]});
            extrude(context, id + "F43", {"entities" : qUnion([Q0, Q1, Q2, Q3]), "operationType" : NewBodyOperationType.REMOVE, "depth" : 13.9 * mm, "offsetDistance" : 25 * mm});
        }
        {
            var Q0;
            Q0=makeQuery(id+"F41.imprint","IMPRINT",FACE,{"disambiguationData":[TD([[makeQuery(id+"F41.imprint","IMPRINT",EDGE,{"derivedFrom":sQuery(id+"F41.wireOp",EDGE,"E104")}),-1.0]])]});
            extrude(context, id + "F44", {"entities" : qUnion([Q0]), "operationType" : NewBodyOperationType.REMOVE, "oppositeDirection" : true, "depth" : 15.3 * mm, "offsetDistance" : 25 * mm, "hasSecondDirection" : true, "secondDirectionOppositeDirection" : true, "secondDirectionDepth" : 5.4 * mm});
        }
    });
